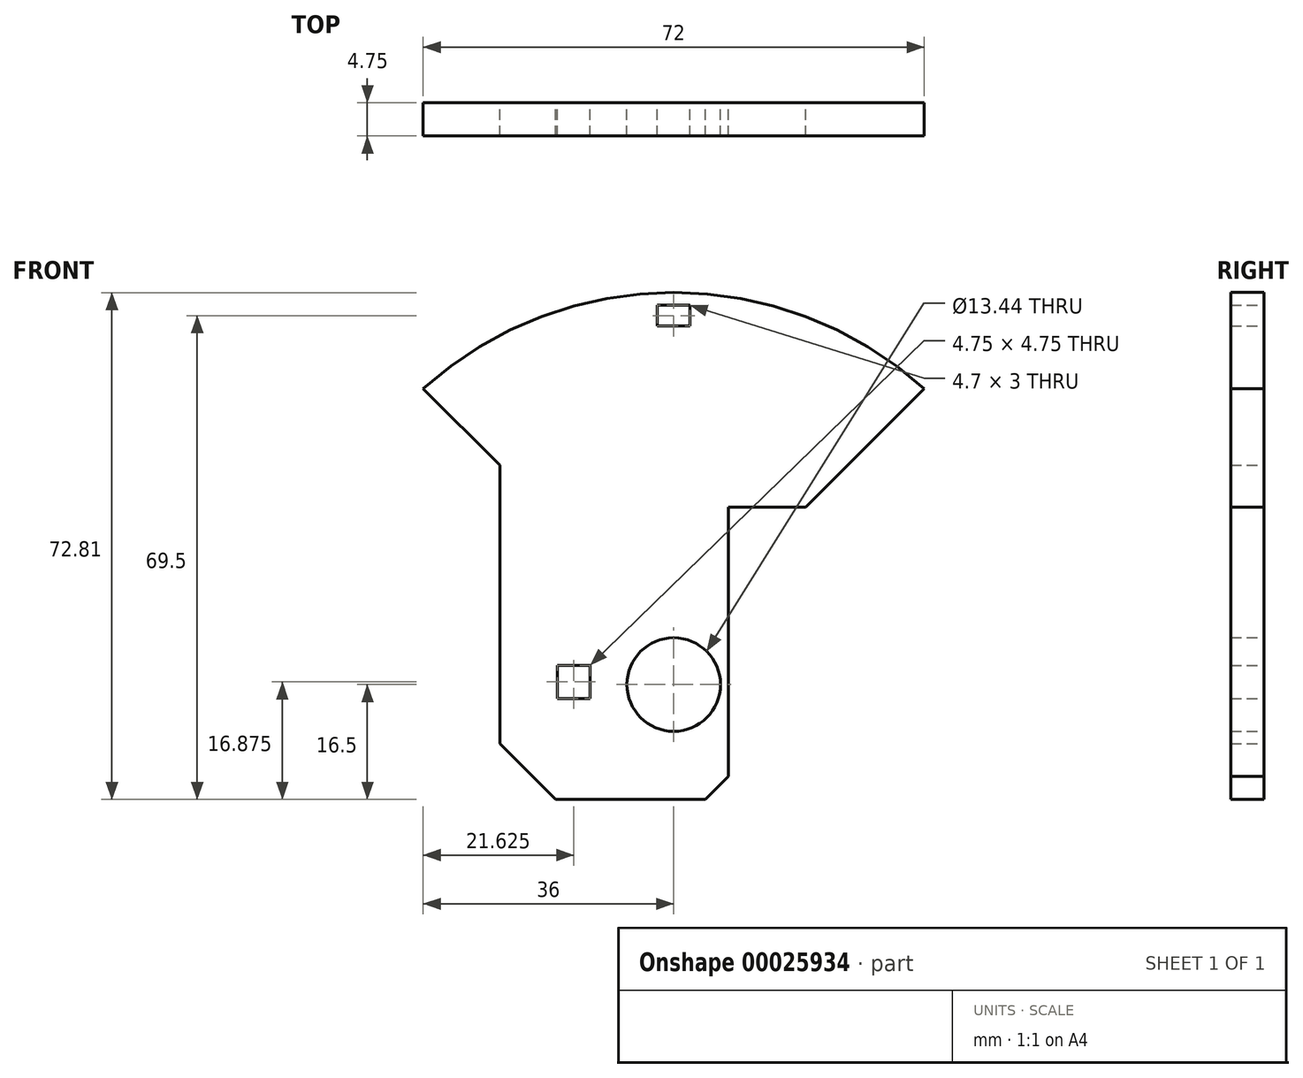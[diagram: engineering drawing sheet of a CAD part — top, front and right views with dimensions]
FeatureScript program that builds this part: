
annotation { "Feature Type Name" : "Feature", "Feature Type Description" : "" }
export const myFeature = defineFeature(function(context is Context, id is Id, definition is map)
    precondition{}
    {
        {
            var Q0;
            Q0=qCreatedBy(makeId("Front.planeOp"),FACE);
            var sketch = newSketch(context, id + "F0", { "sketchPlane" : qUnion([Q0])});
            skLineSegment(sketch, "E0.bottom", {"start": v(0, 0) * mm, "end": v(66.5, 0) * mm, "construction": true});
            skLineSegment(sketch, "E0.top", {"start": v(0, 38) * mm, "end": v(66.5, 38) * mm, "construction": true});
            skLineSegment(sketch, "E0.left", {"start": v(0, 0) * mm, "end": v(0, 23.25) * mm, "construction": true});
            skLineSegment(sketch, "E0.right", {"start": v(66.5, 0) * mm, "end": v(66.5, 38) * mm, "construction": true});
            skLineSegment(sketch, "E1", {"start": v(-4, -8) * mm, "end": v(48.64, -8) * mm, "construction": true});
            skLineSegment(sketch, "E2", {"start": v(48.64, -8) * mm, "end": v(52.64, -4) * mm, "construction": true});
            skLineSegment(sketch, "E3", {"start": v(52.64, -4) * mm, "end": v(102.5, -4) * mm, "construction": true});
            skLineSegment(sketch, "E4", {"start": v(102.5, -4) * mm, "end": v(110.5, -12) * mm});
            skLineSegment(sketch, "E5", {"start": v(110.5, -12) * mm, "end": v(132.04, -12) * mm});
            skLineSegment(sketch, "E6", {"start": v(70.39, 50) * mm, "end": v(-4, 50) * mm, "construction": true});
            skArc(sketch, "E7", {"start": v(-4, 50) * mm, "mid": v(-8.51, 47.97) * mm, "end": v(-10, 43.26) * mm, "construction": true});
            skLineSegment(sketch, "E8", {"start": v(-10, 43.26) * mm, "end": v(-4, -8) * mm, "construction": true});
            skCircle(sketch, "E9", {"center": v(127.5, 4.5) * mm, "radius": 6.72 * mm});
            skLineSegment(sketch, "E10", {"start": v(70.39, 50) * mm, "end": v(73.77, 46.62) * mm, "construction": true});
            skLineSegment(sketch, "E11", {"start": v(73.77, 46.62) * mm, "end": v(73.77, 0) * mm, "construction": true});
            skLineSegment(sketch, "E12", {"start": v(73.77, 0) * mm, "end": v(102.5, 0) * mm, "construction": true});
            skLineSegment(sketch, "E13", {"start": v(102.5, 0) * mm, "end": v(102.5, 36) * mm});
            skLineSegment(sketch, "E14", {"start": v(135.38, 30) * mm, "end": v(135.38, -8.67) * mm});
            skLineSegment(sketch, "E15", {"start": v(135.38, -8.67) * mm, "end": v(132.04, -12) * mm});
            skLineSegment(sketch, "E16.bottom", {"start": v(-1.5, 38) * mm, "end": v(-6.25, 38) * mm, "construction": true});
            skLineSegment(sketch, "E16.top", {"start": v(-1.5, 33.25) * mm, "end": v(-6.25, 33.25) * mm, "construction": true});
            skLineSegment(sketch, "E16.left", {"start": v(-1.5, 38) * mm, "end": v(-1.5, 33.25) * mm, "construction": true});
            skLineSegment(sketch, "E16.right", {"start": v(-6.25, 38) * mm, "end": v(-6.25, 33.25) * mm, "construction": true});
            skLineSegment(sketch, "E17.bottom", {"start": v(110.75, 7.25) * mm, "end": v(115.5, 7.25) * mm});
            skLineSegment(sketch, "E17.top", {"start": v(110.75, 2.5) * mm, "end": v(115.5, 2.5) * mm});
            skLineSegment(sketch, "E17.left", {"start": v(110.75, 7.25) * mm, "end": v(110.75, 2.5) * mm});
            skLineSegment(sketch, "E17.right", {"start": v(115.5, 7.25) * mm, "end": v(115.5, 2.5) * mm});
            skLineSegment(sketch, "E18", {"start": v(0, 28) * mm, "end": v(-4.75, 28) * mm, "construction": true});
            skLineSegment(sketch, "E19", {"start": v(-4.75, 28) * mm, "end": v(-4.75, 23.25) * mm, "construction": true});
            skLineSegment(sketch, "E20", {"start": v(-4.75, 23.25) * mm, "end": v(0, 23.25) * mm, "construction": true});
            skLineSegment(sketch, "E21.trimOffspring", {"start": v(0, 28) * mm, "end": v(0, 38) * mm, "construction": true});
            skLineSegment(sketch, "E22", {"start": v(102.5, 0) * mm, "end": v(86.5, 0) * mm, "construction": true});
            skLineSegment(sketch, "E23", {"start": v(86.5, 0) * mm, "end": v(86.5, -4) * mm, "construction": true});
            skLineSegment(sketch, "E24", {"start": v(86.5, -4) * mm, "end": v(102.5, -4) * mm, "construction": true});
            skLineSegment(sketch, "E25", {"start": v(102.5, 0) * mm, "end": v(102.5, -4) * mm});
            skLineSegment(sketch, "E26", {"start": v(102.5, 36) * mm, "end": v(91.5, 47) * mm});
            skArc(sketch, "E27", {"start": v(91.5, 47) * mm, "mid": v(127.5, 60.81) * mm, "end": v(163.5, 47) * mm});
            skLineSegment(sketch, "E28", {"start": v(163.5, 47) * mm, "end": v(146.5, 30) * mm});
            skLineSegment(sketch, "E29", {"start": v(146.5, 30) * mm, "end": v(135.38, 30) * mm});
            skLineSegment(sketch, "E30.rect.bottom", {"start": v(125.15, 59) * mm, "end": v(129.85, 59) * mm});
            skLineSegment(sketch, "E30.rect.top", {"start": v(125.15, 56) * mm, "end": v(129.85, 56) * mm});
            skLineSegment(sketch, "E30.rect.left", {"start": v(125.15, 59) * mm, "end": v(125.15, 56) * mm});
            skLineSegment(sketch, "E30.rect.right", {"start": v(129.85, 59) * mm, "end": v(129.85, 56) * mm});
            skPoint(sketch, "E30.rect.middle", {"position": v(127.5, 57.5) * mm});
            skSolve(sketch);
        }
        {
            var Q0;
            Q0=qSketchRegion(id+"F0",true);
            extrude(context, id + "F1", {"entities" : qUnion([Q0]), "depth" : 4.75 * mm});
        }
    });
